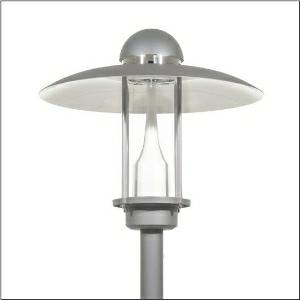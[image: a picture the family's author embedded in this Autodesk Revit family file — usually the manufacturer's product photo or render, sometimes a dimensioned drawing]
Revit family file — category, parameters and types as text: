
# Revit family: city-light_elegance_iq___p1_0a_5xa5265lf14h_79ad
name_source: partatom
category: Lighting Fixtures
units: mm (PartAtom-declared; Revit-internal decimal feet)

## family parameters
Cut with Voids When Loaded = No
Host = Face
Light Source = No
Part Type = Normal
Room Calculation Point = No
Round Connector Dimension = Use Diameter
Shared = No

## types (1)
- --- (1 x LED, 1440 lm, 10 W, 4000K)
    Apparent Load = 10 VA
    CIE Flux Codes = 32 62 91 97 100
    Color Rendering = 70
    Color Temperature = 4000K
    Default Elevation = 1800 mm
    Description = City-Light Elegance iQ, mast luminaire, Module 540 iQ-SR, primary light control with 3 zone facetted reflector, of plastic, silver coated, highly specular, structured, primary optical cover: cover, of PMMA, transparent, light distribution: P1.0a, light emission: direct distribution, primary light characteristic: strongly asymmetric, installation type: post-top, LED, High Power LED, rated luminous flux: 1.440lm, luminous efficacy: 144lm/W, light colour: 740, colour temperature: 4000K, control gear: iQ Street-Remote, control: pre-setting: logarithmic dimming characteristic, Street-Remote, Auto-Match, Temp-Guard, Lumen-Switch, Night-Set, Smart-Wire, Light-Fading, Desk-Remote (wireless, voltage-free reading and setting of iQ features in the workshop via application-optimized NFC function/RFID function), optimised constant luminous flux control (CLO 2.0), with terminal, 6-pole, max. 2.5mm², mains connection: 230..240V, AC, 50/60Hz, start of lifetime: 10W, end of service life: 10W, reduction: 5W, luminaire housing, upper part, of aluminium, coated, Siteco® metallic grey (DB 702S), diameter: 750mm, height: 675mm, spigot size: d x l = 76 x 70mm (post-top) | with reducer (optional accessory) 60 x 70mm, mounting height: 3..5m, post-top mast mounting element, of diecast aluminium, coated, Siteco® metallic grey (DB 702S), Module 540 iQ-SR, traffic white (RAL 9016), equipment: standard, protection rating (complete): IP65, insulation class (complete): insulation class II (safety insulation), certification: CE, ENEC, VDE, packaging unit: 1 piece

Light Distribution: P1.0a
    Height = 675 mm
    Lamp = 1 x LED
    Lamp Light Flux = 1440 lm
    Lamp Power = 10 W
    Lamp count = 1
    Length = 750 mm
    Luminous efficacy = 144 lm/W
    Manufacturer = Siteco
    ModVariant = No
    Model = 5XA5265LF14H
    Number of Poles = 1
    OnlyDefault = Yes
    Power Factor = 1
    Product Name = City-Light Elegance iQ | P1.0a
    Product group = mast luminaire | pylon top
    ProductGroupID = 6100
    Protection Class = Protection class II
    Protection Degree = IP 65
    RLX_Detail_Level = 1
    RLX_Emergency_Light_Flux = 0 lm
    RLX_Emergency_Type = 0
    RLX_Emergency_Type_DB = No
    RlxData = <blob elided: 67389 chars, md5=1c9b31d6>
    Socket = socket
    Standby Power = 0 W
    System Light Flux = 1440 lm
    System Power = 10 W
    Type Comments = factory setting: luminous flux: 100 % | dim-lin: 254 | 401 mA
    Type Image = l_1006912.jpg
    URL = http://relux.com
    VarID = @adj_159718
    Voltage = 0 V
    Weight = 0.00 kg
    Width = 0 mm  [stored 0 ft]

note: [stored X ft] marks values corroborated as IEEE doubles in the binary element streams (Revit-internal decimal feet)

## geometry (parser evidence)
native form markers: Blend x4, Sweep x10
no freeform markers — native parametric forms only
